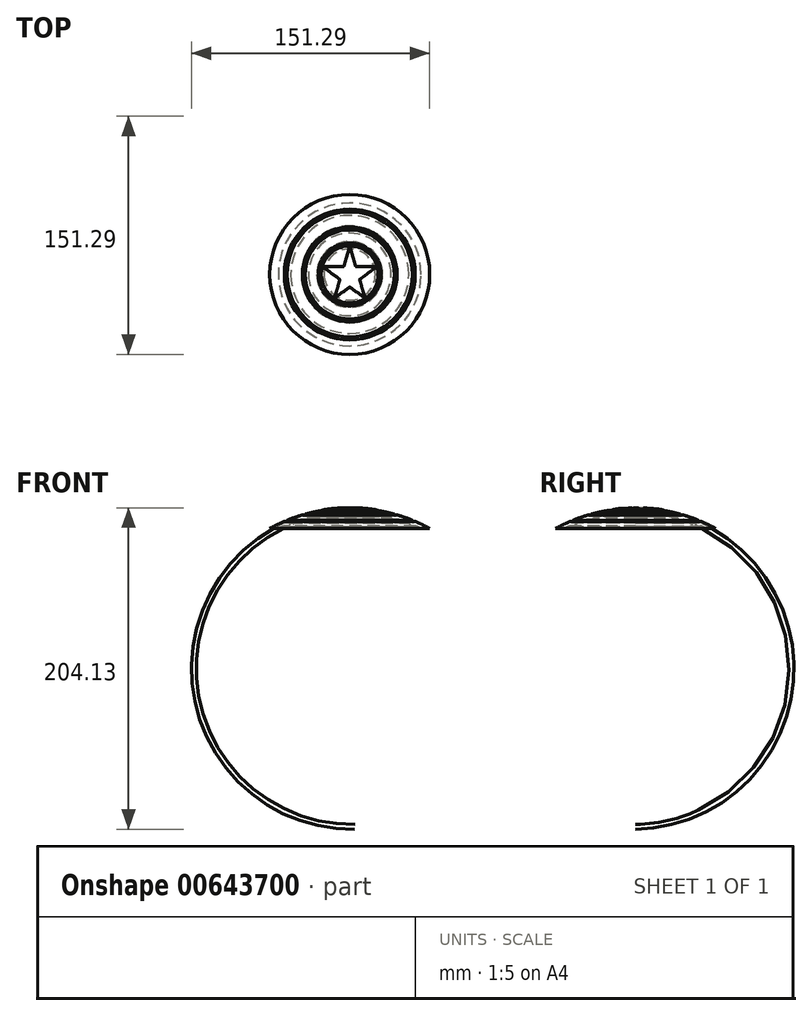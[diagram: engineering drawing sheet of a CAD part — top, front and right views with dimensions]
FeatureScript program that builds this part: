
annotation { "Feature Type Name" : "Feature", "Feature Type Description" : "" }
export const myFeature = defineFeature(function(context is Context, id is Id, definition is map)
    precondition{}
    {
        {
            var Q0;
            Q0=qCreatedBy(makeId("Front.planeOp"),FACE);
            var sketch = newSketch(context, id + "F0", { "sketchPlane" : qUnion([Q0])});
            skLineSegment(sketch, "E0", {"start": v(0, 12.7) * mm, "end": v(0, 0) * mm});
            skLineSegment(sketch, "E1", {"start": v(0, 0) * mm, "end": v(50.8, 0) * mm});
            skArc(sketch, "E2", {"start": v(50.8, 0) * mm, "mid": v(26.23, 9.68) * mm, "end": v(0, 12.7) * mm});
            skSolve(sketch);
        }
        {
            var Q0;
            Q0 = qSketchRegion(id + "F0", true);
            var Q1;
            Q1=sQuery(id+"F0.wireOp",EDGE,"E0");
            revolve(context, id + "F1", {"entities" : qUnion([Q0]), "axis" : qUnion([Q1]), "revolveType" : RevolveType.FULL});
        }
        {
            var Q0;
            Q0=qCreatedBy(makeId("Front.planeOp"),FACE);
            var sketch = newSketch(context, id + "F2", { "sketchPlane" : qUnion([Q0])});
            skLineSegment(sketch, "E3.0", {"start": v(0, 12.7) * mm, "end": v(0, 0) * mm, "construction": true});
            skArc(sketch, "E3.1", {"start": v(50.8, 0) * mm, "mid": v(26.23, 9.68) * mm, "end": v(0, 12.7) * mm, "construction": true});
            skLineSegment(sketch, "E3.2", {"start": v(0, 0) * mm, "end": v(50.8, 0) * mm, "construction": true});
            skCircle(sketch, "E4", {"center": v(19.05, 11.2) * mm, "radius": 0.95 * mm});
            skCircle(sketch, "E5", {"center": v(29.21, 8.89) * mm, "radius": 0.95 * mm});
            skCircle(sketch, "E6", {"center": v(40.64, 4.9) * mm, "radius": 0.95 * mm});
            skSolve(sketch);
        }
        {
            var Q0;
            Q0 = qSketchRegion(id + "F2", true);
            var Q1;
            Q1=sQuery(id+"F0.wireOp",EDGE,"E0");
            revolve(context, id + "F3", {"operationType" : NewBodyOperationType.REMOVE, "entities" : qUnion([Q0]), "axis" : qUnion([Q1]), "revolveType" : RevolveType.FULL, "oppositeDirection" : true});
        }
        {
            var Q0;
            Q0=qCreatedBy(makeId("Top.planeOp"),FACE);
            cPlane(context, id + "F4", {"entities" : qUnion([Q0]), "cplaneType" : CPlaneType.OFFSET, "offset" : 12.7 * mm, "width" : 152.4 * mm, "height" : 152.4 * mm});
        }
        {
            var Q0;
            Q0=qCreatedBy(id+"F4.planeOp",FACE);
            var sketch = newSketch(context, id + "F5", { "sketchPlane" : qUnion([Q0])});
            skLineSegment(sketch, "E7", {"start": v(0, 18.11) * mm, "end": v(0, -18.11) * mm, "construction": true});
            skCircle(sketch, "E8.0", {"center": v(0, 0) * mm, "radius": 18.11 * mm, "construction": true});
            skLineSegment(sketch, "E9", {"start": v(0, 18.11) * mm, "end": v(-3.82, 5.08) * mm});
            skLineSegment(sketch, "E10", {"start": v(-9.79, -15.24) * mm, "end": v(0, -7.92) * mm});
            skLineSegment(sketch, "E11", {"start": v(17.38, 5.08) * mm, "end": v(3.82, 5.08) * mm});
            skLineSegment(sketch, "E12", {"start": v(-17.38, 5.08) * mm, "end": v(-6.26, -3.24) * mm});
            skLineSegment(sketch, "E13", {"start": v(9.79, -15.24) * mm, "end": v(6.26, -3.24) * mm});
            skLineSegment(sketch, "E14.trimOffspring", {"start": v(-3.82, 5.08) * mm, "end": v(-17.38, 5.08) * mm});
            skLineSegment(sketch, "E15.trimOffspring", {"start": v(-6.26, -3.24) * mm, "end": v(-9.79, -15.24) * mm});
            skLineSegment(sketch, "E16.trimOffspring", {"start": v(3.82, 5.08) * mm, "end": v(0, 18.11) * mm});
            skLineSegment(sketch, "E17.trimOffspring", {"start": v(6.26, -3.24) * mm, "end": v(17.38, 5.08) * mm});
            skLineSegment(sketch, "E18.trimOffspring", {"start": v(0, -7.92) * mm, "end": v(9.79, -15.24) * mm});
            skSolve(sketch);
        }
        {
            var Q0;
            Q0=makeQuery(id+"F1.opRevolve","SWEPT_FACE",FACE,{"disambiguationData":[OSD([sQuery(id+"F0.wireOp",EDGE,"E1")])]});
            shell(context, id + "F6", {"entities" : qUnion([Q0]), "thickness" : 2.54 * mm});
        }
        {
            var Q0;
            Q0 = qSketchRegion(id + "F5", true);
            var Q1;
            Q1=makeQuery(id+"F1.opRevolve","SWEPT_BODY",BODY,{"disambiguationData":[OSD([sQuery(id+"F0.wireOp",EDGE,"E0"),sQuery(id+"F0.wireOp",EDGE,"E1"),sQuery(id+"F0.wireOp",EDGE,"E2")])]});
            extrude(context, id + "F7", {"entities" : qUnion([Q0]), "operationType" : NewBodyOperationType.ADD, "endBound" : BoundingType.UP_TO_BODY, "oppositeDirection" : true, "depth" : 6.35 * mm, "endBoundEntityBody" : qUnion([Q1]), "offsetDistance" : 25.4 * mm});
        }
        {
            var Q0;
            Q0=qCreatedBy(id+"F4.planeOp",FACE);
            var sketch = newSketch(context, id + "F8", { "sketchPlane" : qUnion([Q0])});
            skLineSegment(sketch, "E19.0", {"start": v(3.82, 5.08) * mm, "end": v(0, 18.11) * mm});
            skLineSegment(sketch, "E19.1", {"start": v(17.38, 5.08) * mm, "end": v(3.82, 5.08) * mm});
            skLineSegment(sketch, "E19.2", {"start": v(6.26, -3.24) * mm, "end": v(17.38, 5.08) * mm});
            skLineSegment(sketch, "E19.3", {"start": v(9.79, -15.24) * mm, "end": v(6.26, -3.24) * mm});
            skLineSegment(sketch, "E19.4", {"start": v(0, -7.92) * mm, "end": v(9.79, -15.24) * mm});
            skLineSegment(sketch, "E19.5", {"start": v(-9.79, -15.24) * mm, "end": v(0, -7.92) * mm});
            skLineSegment(sketch, "E19.6", {"start": v(-6.26, -3.24) * mm, "end": v(-9.79, -15.24) * mm});
            skLineSegment(sketch, "E19.7", {"start": v(-17.38, 5.08) * mm, "end": v(-6.26, -3.24) * mm});
            skLineSegment(sketch, "E19.8", {"start": v(-3.82, 5.08) * mm, "end": v(-17.38, 5.08) * mm});
            skLineSegment(sketch, "E19.9", {"start": v(0, 18.11) * mm, "end": v(-3.82, 5.08) * mm});
            skSolve(sketch);
        }
        {
            var Q0;
            Q0 = qSketchRegion(id + "F8", true);
            extrude(context, id + "F9", {"entities" : qUnion([Q0]), "operationType" : NewBodyOperationType.ADD, "depth" : 2.54 * mm, "offsetDistance" : 25.4 * mm});
        }
        {
            var Q0;
            Q0=qCreatedBy(makeId("Front.planeOp"),FACE);
            var sketch = newSketch(context, id + "F10", { "sketchPlane" : qUnion([Q0])});
            skArc(sketch, "E20.0", {"start": v(50.8, 0) * mm, "mid": v(26.23, 9.68) * mm, "end": v(0, 12.7) * mm, "construction": true});
            skLineSegment(sketch, "E21", {"start": v(51.58, 0) * mm, "end": v(59.85, 0) * mm});
            skLineSegment(sketch, "E22", {"start": v(59.85, 0) * mm, "end": v(59.85, 35.38) * mm});
            skLineSegment(sketch, "E23", {"start": v(59.85, 35.38) * mm, "end": v(0, 35.38) * mm});
            skLineSegment(sketch, "E24", {"start": v(0, 35.38) * mm, "end": v(0, 13.08) * mm});
            skLineSegment(sketch, "E25", {"start": v(0, 35.38) * mm, "end": v(0, 55.27) * mm, "construction": true});
            skArc(sketch, "E26.0", {"start": v(51.58, 0) * mm, "mid": v(26.66, 9.96) * mm, "end": v(0, 13.08) * mm});
            skArc(sketch, "E27.0", {"start": v(50.78, -0.03) * mm, "mid": v(26.22, 9.65) * mm, "end": v(0, 12.67) * mm});
            skSolve(sketch);
        }
        {
            var Q0;
            Q0 = qSketchRegion(id + "F10", true);
            var Q1;
            Q1=sQuery(id+"F10.wireOp",EDGE,"E25");
            revolve(context, id + "F11", {"operationType" : NewBodyOperationType.REMOVE, "entities" : qUnion([Q0]), "axis" : qUnion([Q1]), "revolveType" : RevolveType.FULL, "oppositeDirection" : true});
        }
        {
            var Q0;
            {var subQ0=sQuery(id+"F5.wireOp",EDGE,"E15.trimOffspring");var subQ1=sQuery(id+"F5.wireOp",EDGE,"E10");Q0=makeQuery(id+"F9.boolean.opBoolean","MERGE",EDGE,{"derivedFrom":[makeQuery(id+"F7.boolean.opBoolean","SPLIT",EDGE,{"disambiguationData":[TD([makeQuery(id+"F1.opRevolve","SWEPT_FACE",FACE,{"disambiguationData":[OSD([sQuery(id+"F0.wireOp",EDGE,"E2")])]}),makeQuery(id+"F3.boolean.opBoolean","COPY",FACE,{"derivedFrom":makeQuery(id+"F3.opRevolve","SWEPT_FACE",FACE,{"disambiguationData":[OSD([sQuery(id+"F2.wireOp",EDGE,"E4")])]})}),makeQuery(id+"F7.opExtrude","CAP_FACE",FACE,{"disambiguationData":[OSD([sQuery(id+"F5.wireOp",EDGE,"E9"),subQ1,sQuery(id+"F5.wireOp",EDGE,"E11"),sQuery(id+"F5.wireOp",EDGE,"E12"),sQuery(id+"F5.wireOp",EDGE,"E13"),sQuery(id+"F5.wireOp",EDGE,"E14.trimOffspring"),subQ0,sQuery(id+"F5.wireOp",EDGE,"E16.trimOffspring"),sQuery(id+"F5.wireOp",EDGE,"E17.trimOffspring"),sQuery(id+"F5.wireOp",EDGE,"E18.trimOffspring")])],"isStart":true}),makeQuery(id+"F7.opExtrude","SWEPT_FACE",FACE,{"disambiguationData":[OSD([subQ1])]}),makeQuery(id+"F7.opExtrude","SWEPT_FACE",FACE,{"disambiguationData":[OSD([subQ0])]})])],"derivedFrom":makeQuery(id+"F7.opExtrude","SWEPT_EDGE",EDGE,{"disambiguationData":[OSD([subQ1,subQ0])]})}),makeQuery(id+"F9.opExtrude","SWEPT_EDGE",EDGE,{"disambiguationData":[OSD([sQuery(id+"F8.wireOp",EDGE,"E19.5"),sQuery(id+"F8.wireOp",EDGE,"E19.6")])]})]});}
            var Q1;
            {var subQ0=sQuery(id+"F5.wireOp",EDGE,"E18.trimOffspring");var subQ1=sQuery(id+"F5.wireOp",EDGE,"E13");Q1=makeQuery(id+"F9.boolean.opBoolean","MERGE",EDGE,{"derivedFrom":[makeQuery(id+"F7.boolean.opBoolean","SPLIT",EDGE,{"disambiguationData":[TD([makeQuery(id+"F1.opRevolve","SWEPT_FACE",FACE,{"disambiguationData":[OSD([sQuery(id+"F0.wireOp",EDGE,"E2")])]}),makeQuery(id+"F3.boolean.opBoolean","COPY",FACE,{"derivedFrom":makeQuery(id+"F3.opRevolve","SWEPT_FACE",FACE,{"disambiguationData":[OSD([sQuery(id+"F2.wireOp",EDGE,"E4")])]})}),makeQuery(id+"F7.opExtrude","CAP_FACE",FACE,{"disambiguationData":[OSD([sQuery(id+"F5.wireOp",EDGE,"E9"),sQuery(id+"F5.wireOp",EDGE,"E10"),sQuery(id+"F5.wireOp",EDGE,"E11"),sQuery(id+"F5.wireOp",EDGE,"E12"),subQ1,sQuery(id+"F5.wireOp",EDGE,"E14.trimOffspring"),sQuery(id+"F5.wireOp",EDGE,"E15.trimOffspring"),sQuery(id+"F5.wireOp",EDGE,"E16.trimOffspring"),sQuery(id+"F5.wireOp",EDGE,"E17.trimOffspring"),subQ0])],"isStart":true}),makeQuery(id+"F7.opExtrude","SWEPT_FACE",FACE,{"disambiguationData":[OSD([subQ1])]}),makeQuery(id+"F7.opExtrude","SWEPT_FACE",FACE,{"disambiguationData":[OSD([subQ0])]})])],"derivedFrom":makeQuery(id+"F7.opExtrude","SWEPT_EDGE",EDGE,{"disambiguationData":[OSD([subQ1,subQ0])]})}),makeQuery(id+"F9.opExtrude","SWEPT_EDGE",EDGE,{"disambiguationData":[OSD([sQuery(id+"F8.wireOp",EDGE,"E19.3"),sQuery(id+"F8.wireOp",EDGE,"E19.4")])]})]});}
            var Q2;
            {var subQ0=sQuery(id+"F5.wireOp",EDGE,"E11");var subQ1=sQuery(id+"F5.wireOp",EDGE,"E17.trimOffspring");Q2=makeQuery(id+"F9.boolean.opBoolean","MERGE",EDGE,{"derivedFrom":[makeQuery(id+"F7.boolean.opBoolean","SPLIT",EDGE,{"disambiguationData":[TD([makeQuery(id+"F1.opRevolve","SWEPT_FACE",FACE,{"disambiguationData":[OSD([sQuery(id+"F0.wireOp",EDGE,"E2")])]}),makeQuery(id+"F3.boolean.opBoolean","COPY",FACE,{"derivedFrom":makeQuery(id+"F3.opRevolve","SWEPT_FACE",FACE,{"disambiguationData":[OSD([sQuery(id+"F2.wireOp",EDGE,"E4")])]})}),makeQuery(id+"F7.opExtrude","CAP_FACE",FACE,{"disambiguationData":[OSD([sQuery(id+"F5.wireOp",EDGE,"E9"),sQuery(id+"F5.wireOp",EDGE,"E10"),subQ0,sQuery(id+"F5.wireOp",EDGE,"E12"),sQuery(id+"F5.wireOp",EDGE,"E13"),sQuery(id+"F5.wireOp",EDGE,"E14.trimOffspring"),sQuery(id+"F5.wireOp",EDGE,"E15.trimOffspring"),sQuery(id+"F5.wireOp",EDGE,"E16.trimOffspring"),subQ1,sQuery(id+"F5.wireOp",EDGE,"E18.trimOffspring")])],"isStart":true}),makeQuery(id+"F7.opExtrude","SWEPT_FACE",FACE,{"disambiguationData":[OSD([subQ0])]}),makeQuery(id+"F7.opExtrude","SWEPT_FACE",FACE,{"disambiguationData":[OSD([subQ1])]})])],"derivedFrom":makeQuery(id+"F7.opExtrude","SWEPT_EDGE",EDGE,{"disambiguationData":[OSD([subQ0,subQ1])]})}),makeQuery(id+"F9.opExtrude","SWEPT_EDGE",EDGE,{"disambiguationData":[OSD([sQuery(id+"F8.wireOp",EDGE,"E19.1"),sQuery(id+"F8.wireOp",EDGE,"E19.2")])]})]});}
            var Q3;
            {var subQ0=sQuery(id+"F5.wireOp",EDGE,"E16.trimOffspring");var subQ1=sQuery(id+"F5.wireOp",EDGE,"E9");Q3=makeQuery(id+"F9.boolean.opBoolean","MERGE",EDGE,{"derivedFrom":[makeQuery(id+"F7.boolean.opBoolean","SPLIT",EDGE,{"disambiguationData":[TD([makeQuery(id+"F1.opRevolve","SWEPT_FACE",FACE,{"disambiguationData":[OSD([sQuery(id+"F0.wireOp",EDGE,"E2")])]}),makeQuery(id+"F3.boolean.opBoolean","COPY",FACE,{"derivedFrom":makeQuery(id+"F3.opRevolve","SWEPT_FACE",FACE,{"disambiguationData":[OSD([sQuery(id+"F2.wireOp",EDGE,"E4")])]})}),makeQuery(id+"F7.opExtrude","SWEPT_FACE",FACE,{"disambiguationData":[OSD([subQ1])]}),makeQuery(id+"F7.opExtrude","CAP_FACE",FACE,{"disambiguationData":[OSD([subQ1,sQuery(id+"F5.wireOp",EDGE,"E10"),sQuery(id+"F5.wireOp",EDGE,"E11"),sQuery(id+"F5.wireOp",EDGE,"E12"),sQuery(id+"F5.wireOp",EDGE,"E13"),sQuery(id+"F5.wireOp",EDGE,"E14.trimOffspring"),sQuery(id+"F5.wireOp",EDGE,"E15.trimOffspring"),subQ0,sQuery(id+"F5.wireOp",EDGE,"E17.trimOffspring"),sQuery(id+"F5.wireOp",EDGE,"E18.trimOffspring")])],"isStart":true}),makeQuery(id+"F7.opExtrude","SWEPT_FACE",FACE,{"disambiguationData":[OSD([subQ0])]})])],"derivedFrom":makeQuery(id+"F7.opExtrude","SWEPT_EDGE",EDGE,{"disambiguationData":[OSD([subQ1,subQ0])]})}),makeQuery(id+"F9.opExtrude","SWEPT_EDGE",EDGE,{"disambiguationData":[OSD([sQuery(id+"F8.wireOp",EDGE,"E19.0"),sQuery(id+"F8.wireOp",EDGE,"E19.9")])]})]});}
            var Q4;
            {var subQ0=sQuery(id+"F5.wireOp",EDGE,"E12");var subQ1=sQuery(id+"F5.wireOp",EDGE,"E14.trimOffspring");Q4=makeQuery(id+"F9.boolean.opBoolean","MERGE",EDGE,{"derivedFrom":[makeQuery(id+"F7.boolean.opBoolean","SPLIT",EDGE,{"disambiguationData":[TD([makeQuery(id+"F1.opRevolve","SWEPT_FACE",FACE,{"disambiguationData":[OSD([sQuery(id+"F0.wireOp",EDGE,"E2")])]}),makeQuery(id+"F3.boolean.opBoolean","COPY",FACE,{"derivedFrom":makeQuery(id+"F3.opRevolve","SWEPT_FACE",FACE,{"disambiguationData":[OSD([sQuery(id+"F2.wireOp",EDGE,"E4")])]})}),makeQuery(id+"F7.opExtrude","CAP_FACE",FACE,{"disambiguationData":[OSD([sQuery(id+"F5.wireOp",EDGE,"E9"),sQuery(id+"F5.wireOp",EDGE,"E10"),sQuery(id+"F5.wireOp",EDGE,"E11"),subQ0,sQuery(id+"F5.wireOp",EDGE,"E13"),subQ1,sQuery(id+"F5.wireOp",EDGE,"E15.trimOffspring"),sQuery(id+"F5.wireOp",EDGE,"E16.trimOffspring"),sQuery(id+"F5.wireOp",EDGE,"E17.trimOffspring"),sQuery(id+"F5.wireOp",EDGE,"E18.trimOffspring")])],"isStart":true}),makeQuery(id+"F7.opExtrude","SWEPT_FACE",FACE,{"disambiguationData":[OSD([subQ0])]}),makeQuery(id+"F7.opExtrude","SWEPT_FACE",FACE,{"disambiguationData":[OSD([subQ1])]})])],"derivedFrom":makeQuery(id+"F7.opExtrude","SWEPT_EDGE",EDGE,{"disambiguationData":[OSD([subQ0,subQ1])]})}),makeQuery(id+"F9.opExtrude","SWEPT_EDGE",EDGE,{"disambiguationData":[OSD([sQuery(id+"F8.wireOp",EDGE,"E19.7"),sQuery(id+"F8.wireOp",EDGE,"E19.8")])]})]});}
            fillet(context, id + "F12", {"entities" : qUnion([Q0, Q1, Q2, Q3, Q4]), "radius" : 0.13 * mm, "tangentPropagation" : true, "allowEdgeOverflow" : false});
        }
        {
            var Q0;
            Q0=makeQuery(id+"F9.boolean.opBoolean","MERGE",EDGE,{"derivedFrom":[makeQuery(id+"F7.opExtrude","SWEPT_EDGE",EDGE,{"disambiguationData":[OSD([sQuery(id+"F5.wireOp",EDGE,"E10"),sQuery(id+"F5.wireOp",EDGE,"E18.trimOffspring")])]}),makeQuery(id+"F9.opExtrude","SWEPT_EDGE",EDGE,{"disambiguationData":[OSD([sQuery(id+"F8.wireOp",EDGE,"E19.4"),sQuery(id+"F8.wireOp",EDGE,"E19.5")])]})]});
            var Q1;
            Q1=makeQuery(id+"F9.boolean.opBoolean","MERGE",EDGE,{"derivedFrom":[makeQuery(id+"F7.opExtrude","SWEPT_EDGE",EDGE,{"disambiguationData":[OSD([sQuery(id+"F5.wireOp",EDGE,"E13"),sQuery(id+"F5.wireOp",EDGE,"E17.trimOffspring")])]}),makeQuery(id+"F9.opExtrude","SWEPT_EDGE",EDGE,{"disambiguationData":[OSD([sQuery(id+"F8.wireOp",EDGE,"E19.2"),sQuery(id+"F8.wireOp",EDGE,"E19.3")])]})]});
            var Q2;
            Q2=makeQuery(id+"F9.boolean.opBoolean","MERGE",EDGE,{"derivedFrom":[makeQuery(id+"F7.opExtrude","SWEPT_EDGE",EDGE,{"disambiguationData":[OSD([sQuery(id+"F5.wireOp",EDGE,"E11"),sQuery(id+"F5.wireOp",EDGE,"E16.trimOffspring")])]}),makeQuery(id+"F9.opExtrude","SWEPT_EDGE",EDGE,{"disambiguationData":[OSD([sQuery(id+"F8.wireOp",EDGE,"E19.0"),sQuery(id+"F8.wireOp",EDGE,"E19.1")])]})]});
            var Q3;
            Q3=makeQuery(id+"F9.boolean.opBoolean","MERGE",EDGE,{"derivedFrom":[makeQuery(id+"F7.opExtrude","SWEPT_EDGE",EDGE,{"disambiguationData":[OSD([sQuery(id+"F5.wireOp",EDGE,"E9"),sQuery(id+"F5.wireOp",EDGE,"E14.trimOffspring")])]}),makeQuery(id+"F9.opExtrude","SWEPT_EDGE",EDGE,{"disambiguationData":[OSD([sQuery(id+"F8.wireOp",EDGE,"E19.8"),sQuery(id+"F8.wireOp",EDGE,"E19.9")])]})]});
            var Q4;
            Q4=makeQuery(id+"F9.boolean.opBoolean","MERGE",EDGE,{"derivedFrom":[makeQuery(id+"F7.opExtrude","SWEPT_EDGE",EDGE,{"disambiguationData":[OSD([sQuery(id+"F5.wireOp",EDGE,"E12"),sQuery(id+"F5.wireOp",EDGE,"E15.trimOffspring")])]}),makeQuery(id+"F9.opExtrude","SWEPT_EDGE",EDGE,{"disambiguationData":[OSD([sQuery(id+"F8.wireOp",EDGE,"E19.6"),sQuery(id+"F8.wireOp",EDGE,"E19.7")])]})]});
            fillet(context, id + "F13", {"entities" : qUnion([Q0, Q1, Q2, Q3, Q4]), "radius" : 0.13 * mm, "tangentPropagation" : true, "allowEdgeOverflow" : false});
        }
    });
